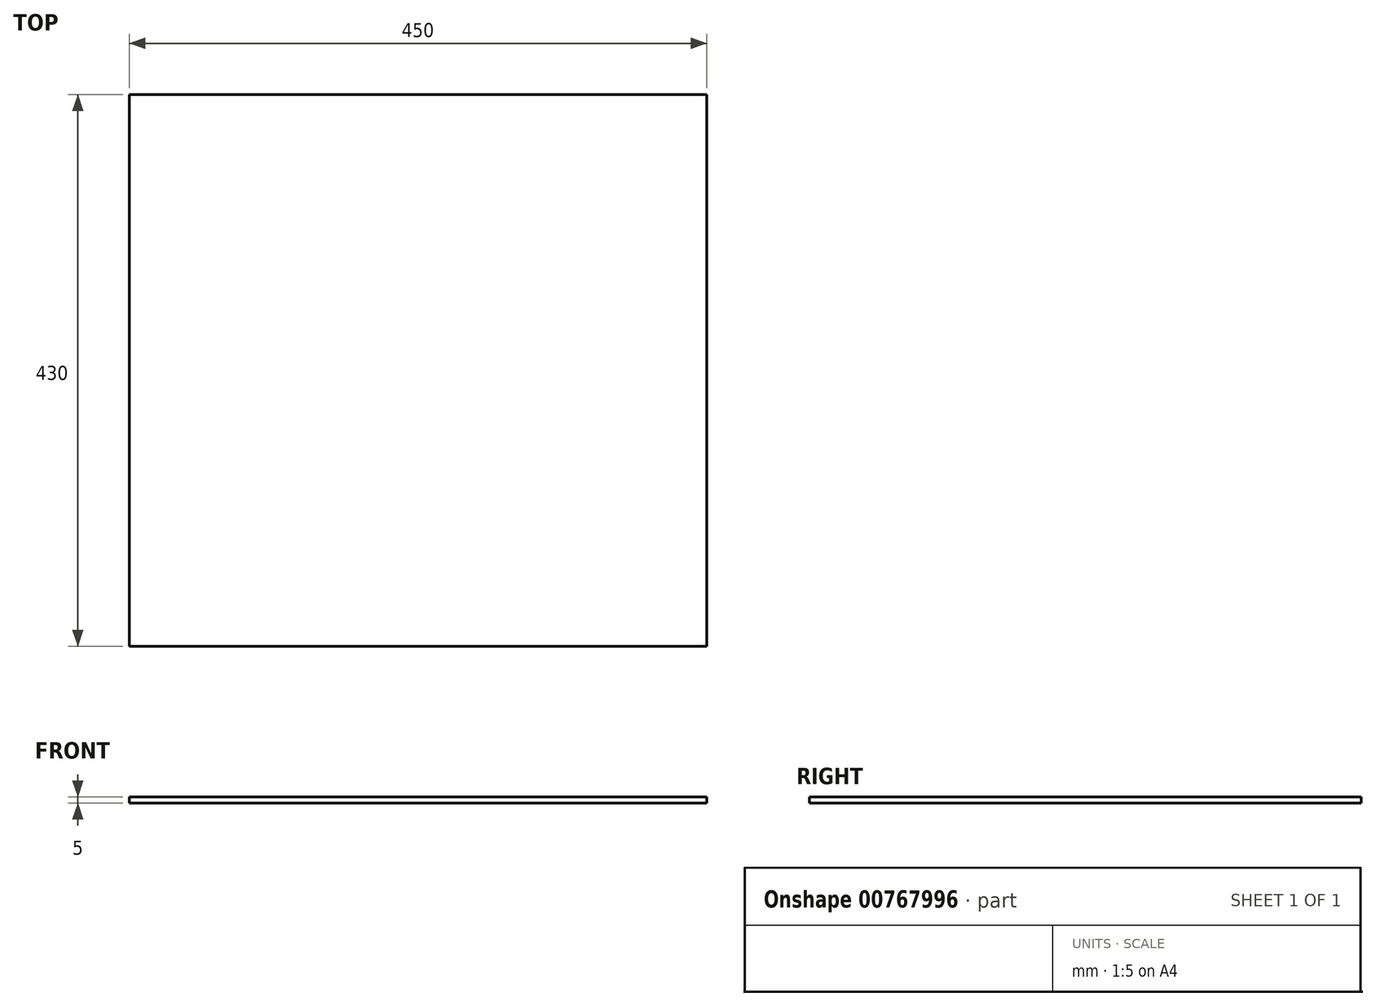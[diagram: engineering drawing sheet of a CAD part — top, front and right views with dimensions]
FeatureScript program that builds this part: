
annotation { "Feature Type Name" : "Feature", "Feature Type Description" : "" }
export const myFeature = defineFeature(function(context is Context, id is Id, definition is map)
    precondition{}
    {
        {
            var Q0;
            Q0=qCreatedBy(makeId("Top.planeOp"),FACE);
            var sketch = newSketch(context, id + "F0", { "sketchPlane" : qUnion([Q0])});
            skLineSegment(sketch, "E0.bottom", {"start": v(-596.02, 304.6) * mm, "end": v(-146.02, 304.6) * mm});
            skLineSegment(sketch, "E0.top", {"start": v(-596.02, -125.4) * mm, "end": v(-146.02, -125.4) * mm});
            skLineSegment(sketch, "E0.left", {"start": v(-596.02, 304.6) * mm, "end": v(-596.02, -125.4) * mm});
            skLineSegment(sketch, "E0.right", {"start": v(-146.02, 304.6) * mm, "end": v(-146.02, -125.4) * mm});
            skSolve(sketch);
        }
        {
            var Q0;
            Q0=makeQuery(id+"F0.imprint","IMPRINT",FACE,{"disambiguationData":[TD([[makeQuery(id+"F0.imprint","IMPRINT",EDGE,{"derivedFrom":sQuery(id+"F0.wireOp",EDGE,"E0.bottom")}),-1.0]])]});
            extrude(context, id + "F1", {"entities" : qUnion([Q0]), "depth" : 5 * mm, "offsetDistance" : 25 * mm});
        }
    });
